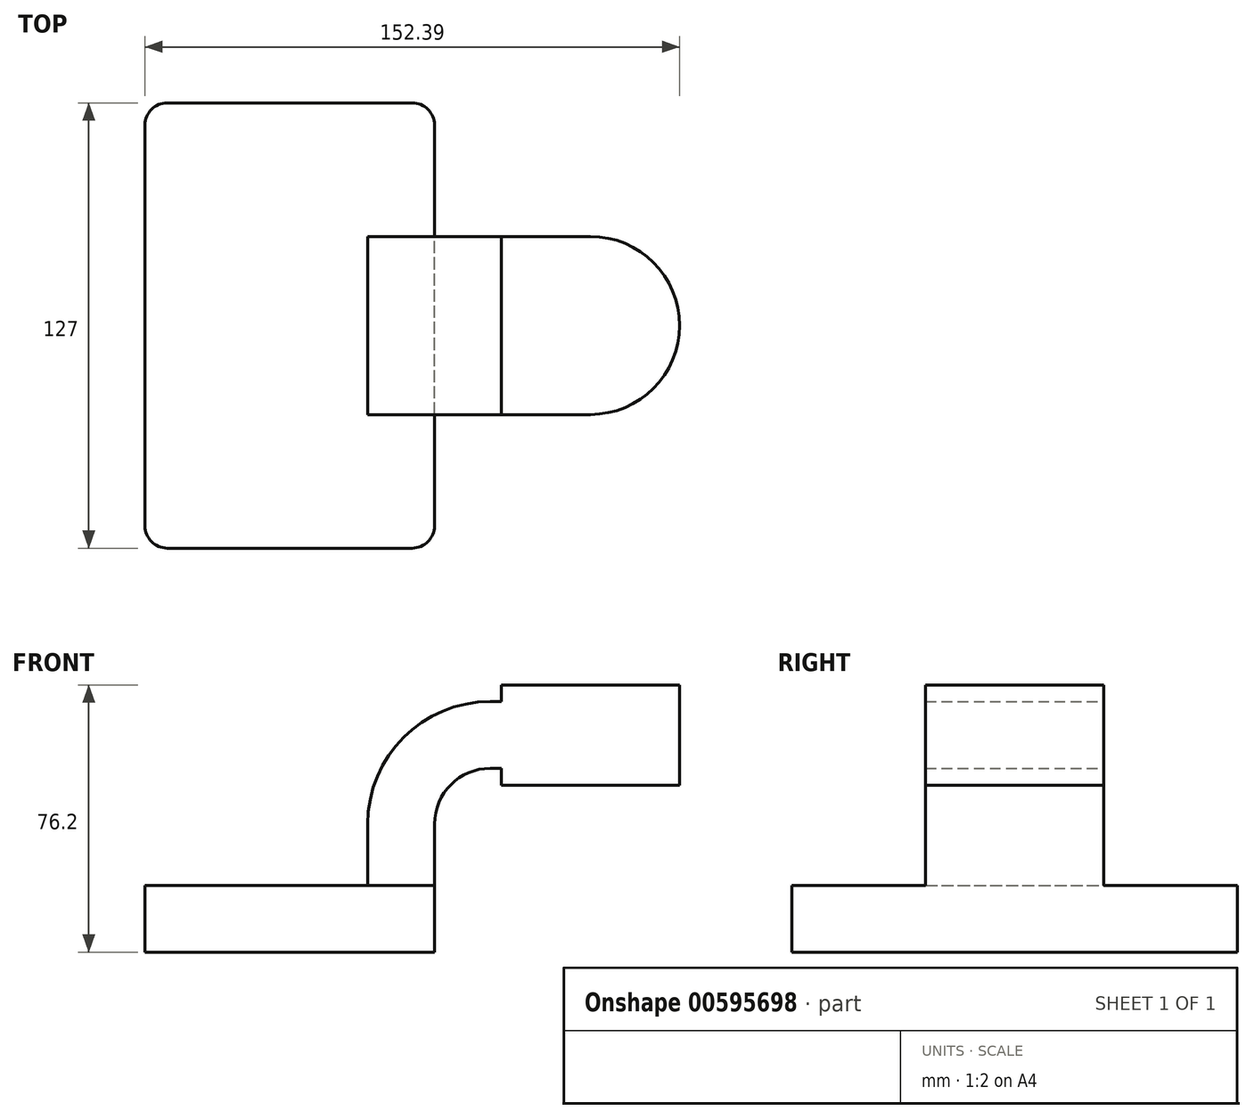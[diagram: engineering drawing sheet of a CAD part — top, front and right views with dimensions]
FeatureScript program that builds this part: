
annotation { "Feature Type Name" : "Feature", "Feature Type Description" : "" }
export const myFeature = defineFeature(function(context is Context, id is Id, definition is map)
    precondition{}
    {
        {
            var Q0;
            Q0=qCreatedBy(makeId("Front.planeOp"),FACE);
            var sketch = newSketch(context, id + "F0", { "sketchPlane" : qUnion([Q0])});
            skLineSegment(sketch, "E0.bottom", {"start": v(41.28, -9.52) * mm, "end": v(-41.27, -9.53) * mm});
            skLineSegment(sketch, "E0.top", {"start": v(41.27, 9.53) * mm, "end": v(-41.27, 9.53) * mm});
            skLineSegment(sketch, "E0.left", {"start": v(41.28, -9.52) * mm, "end": v(41.28, 9.53) * mm});
            skLineSegment(sketch, "E0.right", {"start": v(-41.27, -9.53) * mm, "end": v(-41.27, 9.53) * mm});
            skPoint(sketch, "E0.middle", {"position": v(0, 0) * mm});
            skLineSegment(sketch, "E1.bottom", {"start": v(111.12, 38.1) * mm, "end": v(60.32, 38.1) * mm});
            skLineSegment(sketch, "E1.top", {"start": v(111.12, 66.68) * mm, "end": v(60.32, 66.68) * mm});
            skLineSegment(sketch, "E1.left", {"start": v(111.13, 38.1) * mm, "end": v(111.13, 66.68) * mm});
            skLineSegment(sketch, "E1.right", {"start": v(60.32, 38.1) * mm, "end": v(60.32, 66.68) * mm});
            skPoint(sketch, "E1.middle", {"position": v(85.72, 52.39) * mm});
            skLineSegment(sketch, "E2", {"start": v(41.27, 9.53) * mm, "end": v(41.27, 27) * mm});
            skArc(sketch, "E3", {"start": v(41.27, 27) * mm, "mid": v(45.92, 38.23) * mm, "end": v(57.15, 42.88) * mm});
            skLineSegment(sketch, "E4", {"start": v(57.15, 42.88) * mm, "end": v(85.72, 42.88) * mm});
            skLineSegment(sketch, "E5.0", {"start": v(57.15, 61.93) * mm, "end": v(85.72, 61.93) * mm});
            skArc(sketch, "E5.1", {"start": v(22.23, 27) * mm, "mid": v(32.45, 51.7) * mm, "end": v(57.15, 61.93) * mm});
            skLineSegment(sketch, "E5.2", {"start": v(22.22, 9.53) * mm, "end": v(22.22, 27) * mm});
            skFitSpline(sketch, "E6", {"points": [v(-41.28, 9.52) * mm, v(57.15, 61.93) * mm], "startDerivative": vector(40.2, 137.6) * mm, "endDerivative": vector(150.17, -9.54) * mm});
            skLineSegment(sketch, "E7", {"start": v(85.72, 38.1) * mm, "end": v(85.72, 66.68) * mm});
            skSolve(sketch);
        }
        {
            var Q0;
            Q0=makeQuery(id+"F0.imprint","IMPRINT",FACE,{"disambiguationData":[TD([[makeQuery(id+"F0.imprint","IMPRINT",EDGE,{"derivedFrom":sQuery(id+"F0.wireOp",EDGE,"E0.bottom")}),-1.0]])]});
            extrude(context, id + "F1", {"entities" : qUnion([Q0]), "endBound" : BoundingType.SYMMETRIC, "depth" : 127 * mm, "offsetDistance" : 25.4 * mm});
        }
        {
            var Q0;
            {var subQ1=sQuery(id+"F0.wireOp",EDGE,"E2");Q0=makeQuery(id+"F0.imprint","IMPRINT",FACE,{"disambiguationData":[TD([[makeQuery(id+"F0.imprint","IMPRINT",EDGE,{"derivedFrom":subQ1}),1.0]])]});}
            var Q1;
            {var subQ0=sQuery(id+"F0.wireOp",EDGE,"E4");var subQ1=sQuery(id+"F0.wireOp",EDGE,"E1.right");var subQ2=makeQuery(id+"F0.imprint","INTERSECT",VERTEX,{"derivedFrom":[subQ1,subQ0]});Q1=makeQuery(id+"F0.imprint","IMPRINT",FACE,{"disambiguationData":[TD([[makeQuery(id+"F0.imprint","IMPRINT",EDGE,{"disambiguationData":[TD([[subQ2,-1.0]])],"derivedFrom":subQ1}),-1.0]])]});}
            extrude(context, id + "F2", {"entities" : qUnion([Q0, Q1]), "operationType" : NewBodyOperationType.ADD, "endBound" : BoundingType.SYMMETRIC, "depth" : 50.8 * mm, "offsetDistance" : 25.4 * mm});
        }
        {
            var Q0;
            Q0=makeQuery(id+"F0.imprint","IMPRINT",FACE,{"disambiguationData":[TD([[makeQuery(id+"F0.imprint","IMPRINT",EDGE,{"derivedFrom":sQuery(id+"F0.wireOp",EDGE,"E5.1")}),1.0]])]});
            extrude(context, id + "F3", {"entities" : qUnion([Q0]), "operationType" : NewBodyOperationType.ADD, "endBound" : BoundingType.SYMMETRIC, "depth" : 15.88 * mm, "offsetDistance" : 25.4 * mm});
        }
        {
            var Q0;
            {var subQ0=sQuery(id+"F0.wireOp",EDGE,"E1.left");Q0=makeQuery(id+"F0.imprint","IMPRINT",FACE,{"disambiguationData":[TD([[makeQuery(id+"F0.imprint","IMPRINT",EDGE,{"derivedFrom":subQ0}),1.0]])]});}
            var Q1;
            Q1=sQuery(id+"F0.wireOp",EDGE,"E7");
            revolve(context, id + "F4", {"operationType" : NewBodyOperationType.ADD, "entities" : qUnion([Q0]), "axis" : qUnion([Q1]), "revolveType" : RevolveType.FULL});
        }
        {
            var Q0;
            Q0=makeQuery(id+"F1.opExtrude","CAP_EDGE",EDGE,{"disambiguationData":[OSD([sQuery(id+"F0.wireOp",EDGE,"E0.right")])],"isStart":false});
            var Q1;
            Q1=makeQuery(id+"F1.opExtrude","CAP_EDGE",EDGE,{"disambiguationData":[OSD([sQuery(id+"F0.wireOp",EDGE,"E0.left")])],"isStart":false});
            var Q2;
            Q2=makeQuery(id+"F1.opExtrude","CAP_EDGE",EDGE,{"disambiguationData":[OSD([sQuery(id+"F0.wireOp",EDGE,"E0.left")])],"isStart":true});
            var Q3;
            Q3=makeQuery(id+"F1.opExtrude","CAP_EDGE",EDGE,{"disambiguationData":[OSD([sQuery(id+"F0.wireOp",EDGE,"E0.right")])],"isStart":true});
            fillet(context, id + "F5", {"entities" : qUnion([Q0, Q1, Q2, Q3]), "radius" : 6.35 * mm, "tangentPropagation" : true, "allowEdgeOverflow" : false});
        }
    });
